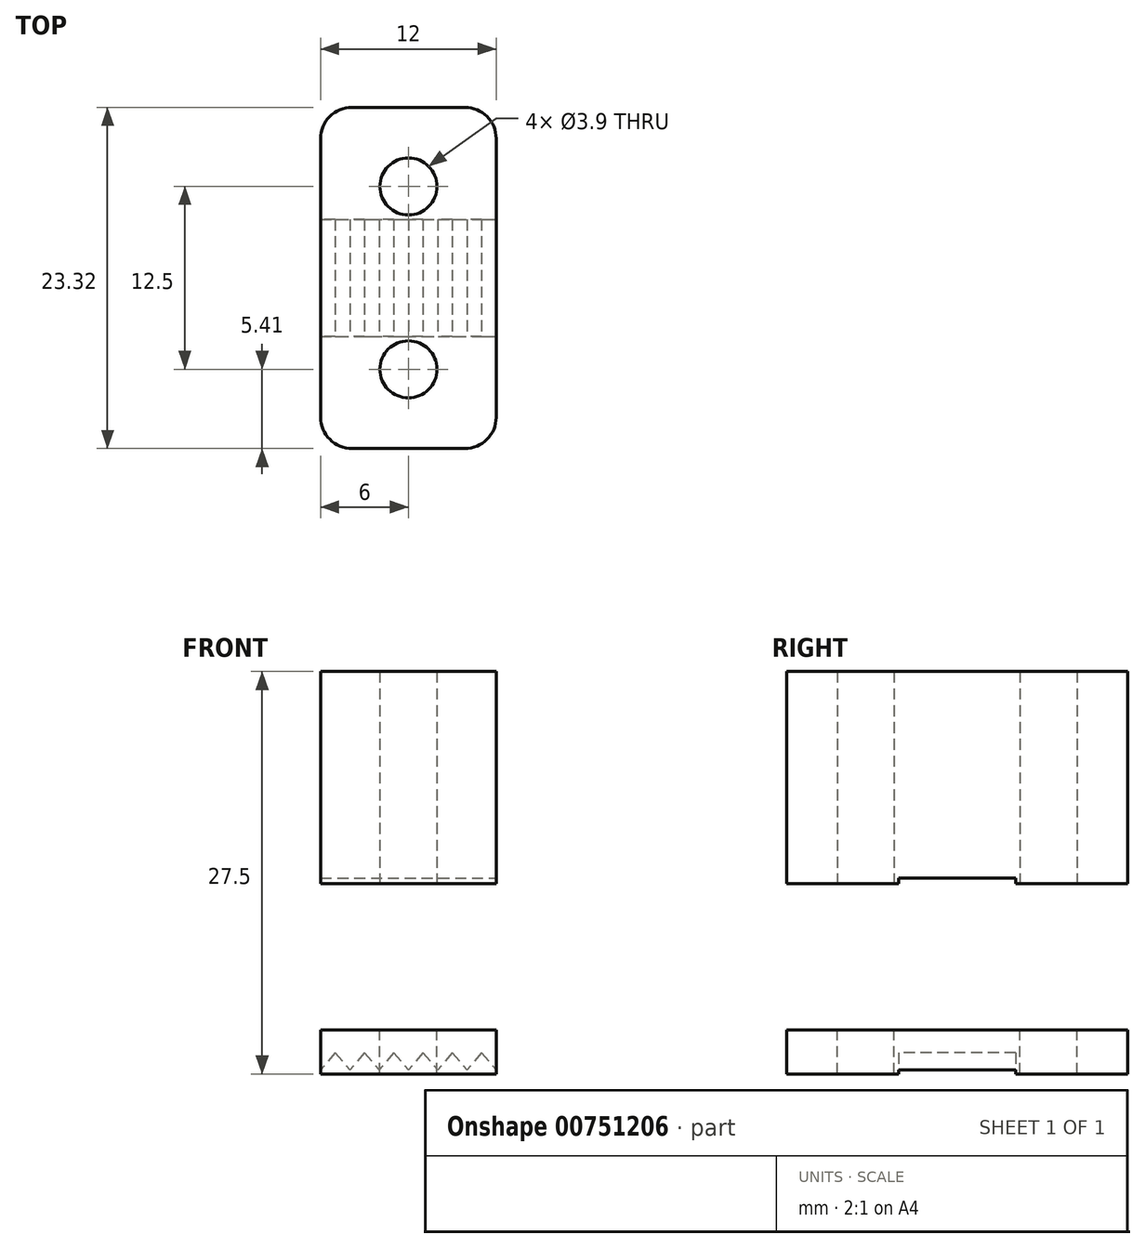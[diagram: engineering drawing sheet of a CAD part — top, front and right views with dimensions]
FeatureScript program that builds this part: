
annotation { "Feature Type Name" : "Feature", "Feature Type Description" : "" }
export const myFeature = defineFeature(function(context is Context, id is Id, definition is map)
    precondition{}
    {
        {
            var Q0;
            Q0=qCreatedBy(makeId("Top.planeOp"),FACE);
            var sketch = newSketch(context, id + "F0", { "sketchPlane" : qUnion([Q0])});
            skCircle(sketch, "E0", {"center": v(0, 6.25) * mm, "radius": 1.95 * mm});
            skLineSegment(sketch, "E1.bottom", {"start": v(-3.85, 11.66) * mm, "end": v(3.85, 11.66) * mm});
            skLineSegment(sketch, "E1.top", {"start": v(-6, 0) * mm, "end": v(6, 0) * mm});
            skLineSegment(sketch, "E1.left", {"start": v(-6, 9.52) * mm, "end": v(-6, 0) * mm});
            skLineSegment(sketch, "E1.right", {"start": v(6, 9.52) * mm, "end": v(6, 0) * mm});
            skPoint(sketch, "E2.visualSharp", {"position": v(-6, 11.66) * mm});
            skArc(sketch, "E2.filletArc", {"start": v(-3.85, 11.66) * mm, "mid": v(-5.37, 11.03) * mm, "end": v(-6, 9.52) * mm});
            skPoint(sketch, "E3.visualSharp", {"position": v(6, 11.66) * mm});
            skArc(sketch, "E3.filletArc", {"start": v(6, 9.52) * mm, "mid": v(5.37, 11.03) * mm, "end": v(3.85, 11.66) * mm});
            skSolve(sketch);
        }
        {
            var Q0;
            Q0=makeQuery(id+"F0.imprint","IMPRINT",FACE,{"disambiguationData":[TD([[makeQuery(id+"F0.imprint","IMPRINT",EDGE,{"derivedFrom":sQuery(id+"F0.wireOp",EDGE,"E0")}),-1.0]])]});
            extrude(context, id + "F1", {"entities" : qUnion([Q0]), "depth" : 6.5 * mm});
        }
        {
            var Q0;
            Q0=makeQuery(id+"F1.opExtrude","SWEPT_BODY",BODY,{"disambiguationData":[OSD([sQuery(id+"F0.wireOp",EDGE,"E0"),sQuery(id+"F0.wireOp",EDGE,"E1.bottom"),sQuery(id+"F0.wireOp",EDGE,"E1.top"),sQuery(id+"F0.wireOp",EDGE,"E1.left"),sQuery(id+"F0.wireOp",EDGE,"E1.right"),sQuery(id+"F0.wireOp",EDGE,"E2.filletArc"),sQuery(id+"F0.wireOp",EDGE,"E3.filletArc")])]});
            var Q1;
            Q1=qCreatedBy(makeId("Front.planeOp"),FACE);
            mirror(context, id + "F2", {"operationType" : NewBodyOperationType.ADD, "entities" : qUnion([Q0]), "mirrorPlane" : qUnion([Q1])});
        }
        {
            var Q0;
            Q0=qCreatedBy(makeId("Top.planeOp"),FACE);
            cPlane(context, id + "F3", {"entities" : qUnion([Q0]), "cplaneType" : CPlaneType.OFFSET, "offset" : 10 * mm, "oppositeDirection" : true, "width" : 150 * mm, "height" : 150 * mm});
        }
        {
            var Q0;
            Q0=qCreatedBy(id+"F3.planeOp",FACE);
            var sketch = newSketch(context, id + "F4", { "sketchPlane" : qUnion([Q0])});
            skCircle(sketch, "E4.0", {"center": v(0, -6.25) * mm, "radius": 1.95 * mm});
            skCircle(sketch, "E5.0", {"center": v(0, 6.25) * mm, "radius": 1.95 * mm});
            skLineSegment(sketch, "E6.0", {"start": v(-6, 9.52) * mm, "end": v(-6, -9.52) * mm});
            skArc(sketch, "E7.0", {"start": v(-3.85, -11.66) * mm, "mid": v(-5.37, -11.03) * mm, "end": v(-6, -9.52) * mm});
            skLineSegment(sketch, "E8.0", {"start": v(-3.85, -11.66) * mm, "end": v(3.85, -11.66) * mm});
            skPoint(sketch, "E9.0", {"position": v(5.37, -11.03) * mm});
            skArc(sketch, "E10.0", {"start": v(6, -9.52) * mm, "mid": v(5.37, -11.03) * mm, "end": v(3.85, -11.66) * mm});
            skLineSegment(sketch, "E11.0", {"start": v(6, 9.52) * mm, "end": v(6, -9.52) * mm});
            skArc(sketch, "E12.0", {"start": v(6, 9.52) * mm, "mid": v(5.37, 11.03) * mm, "end": v(3.85, 11.66) * mm});
            skLineSegment(sketch, "E13.0", {"start": v(-3.85, 11.66) * mm, "end": v(3.85, 11.66) * mm});
            skArc(sketch, "E14.0", {"start": v(-3.85, 11.66) * mm, "mid": v(-5.37, 11.03) * mm, "end": v(-6, 9.52) * mm});
            skSolve(sketch);
        }
        {
            var Q0;
            Q0=makeQuery(id+"F4.imprint","IMPRINT",FACE,{"disambiguationData":[TD([[makeQuery(id+"F4.imprint","IMPRINT",EDGE,{"derivedFrom":sQuery(id+"F4.wireOp",EDGE,"E4.0")}),-1.0]])]});
            extrude(context, id + "F5", {"entities" : qUnion([Q0]), "oppositeDirection" : true, "depth" : 3 * mm});
        }
        {
            var Q0;
            Q0=qCreatedBy(makeId("Front.planeOp"),FACE);
            var sketch = newSketch(context, id + "F6", { "sketchPlane" : qUnion([Q0])});
            skLineSegment(sketch, "E15.0", {"start": v(-6, -13) * mm, "end": v(-6, -12.73) * mm});
            skLineSegment(sketch, "E16.bottom", {"start": v(-6, -13) * mm, "end": v(-4, -13) * mm});
            skLineSegment(sketch, "E16.right", {"start": v(-4, -13) * mm, "end": v(-4, -12.73) * mm});
            skPoint(sketch, "E17", {"position": v(-5, -11.55) * mm});
            skLineSegment(sketch, "E18", {"start": v(-5, -11.55) * mm, "end": v(-4, -12.73) * mm});
            skLineSegment(sketch, "E19", {"start": v(-5, -11.55) * mm, "end": v(-6, -12.73) * mm});
            skPoint(sketch, "E20.orphan", {"position": v(-4, -11.55) * mm});
            skLineSegment(sketch, "E21.trimOffspring", {"start": v(-6, -11.55) * mm, "end": v(-6, -10) * mm});
            skLineSegment(sketch, "E22.1.0.0", {"start": v(-3, -11.55) * mm, "end": v(-2, -12.73) * mm});
            skLineSegment(sketch, "E22.1.0.1", {"start": v(-3, -11.55) * mm, "end": v(-4, -12.73) * mm});
            skLineSegment(sketch, "E22.1.0.3", {"start": v(-4, -13) * mm, "end": v(-2, -13) * mm});
            skLineSegment(sketch, "E22.1.0.4", {"start": v(-2, -13) * mm, "end": v(-2, -12.73) * mm});
            skLineSegment(sketch, "E22.2.0.0", {"start": v(-1, -11.55) * mm, "end": v(0, -12.73) * mm});
            skLineSegment(sketch, "E22.2.0.1", {"start": v(-1, -11.55) * mm, "end": v(-2, -12.73) * mm});
            skLineSegment(sketch, "E22.2.0.2", {"start": v(-2, -13) * mm, "end": v(-2, -12.73) * mm});
            skLineSegment(sketch, "E22.2.0.3", {"start": v(-2, -13) * mm, "end": v(0, -13) * mm});
            skLineSegment(sketch, "E22.2.0.4", {"start": v(0, -13) * mm, "end": v(0, -12.73) * mm});
            skLineSegment(sketch, "E22.3.0.0", {"start": v(1, -11.55) * mm, "end": v(2, -12.73) * mm});
            skLineSegment(sketch, "E22.3.0.1", {"start": v(1, -11.55) * mm, "end": v(0, -12.73) * mm});
            skLineSegment(sketch, "E22.3.0.2", {"start": v(0, -13) * mm, "end": v(0, -12.73) * mm});
            skLineSegment(sketch, "E22.3.0.3", {"start": v(0, -13) * mm, "end": v(2, -13) * mm});
            skLineSegment(sketch, "E22.3.0.4", {"start": v(2, -13) * mm, "end": v(2, -12.73) * mm});
            skLineSegment(sketch, "E22.4.0.0", {"start": v(3, -11.55) * mm, "end": v(4, -12.73) * mm});
            skLineSegment(sketch, "E22.4.0.1", {"start": v(3, -11.55) * mm, "end": v(2, -12.73) * mm});
            skLineSegment(sketch, "E22.4.0.2", {"start": v(2, -13) * mm, "end": v(2, -12.73) * mm});
            skLineSegment(sketch, "E22.4.0.3", {"start": v(2, -13) * mm, "end": v(4, -13) * mm});
            skLineSegment(sketch, "E22.4.0.4", {"start": v(4, -13) * mm, "end": v(4, -12.73) * mm});
            skLineSegment(sketch, "E22.5.0.0", {"start": v(5, -11.55) * mm, "end": v(6, -12.73) * mm});
            skLineSegment(sketch, "E22.5.0.1", {"start": v(5, -11.55) * mm, "end": v(4, -12.73) * mm});
            skLineSegment(sketch, "E22.5.0.2", {"start": v(4, -13) * mm, "end": v(4, -12.73) * mm});
            skLineSegment(sketch, "E22.5.0.3", {"start": v(4, -13) * mm, "end": v(6, -13) * mm});
            skLineSegment(sketch, "E22.5.0.4", {"start": v(6, -13) * mm, "end": v(6, -12.73) * mm});
            skLineSegment(sketch, "E22.direction1", {"start": v(-4, -12.73) * mm, "end": v(-2, -12.73) * mm, "construction": true});
            skSolve(sketch);
        }
        {
            var Q0;
            Q0=qSketchRegion(id+"F6",true);
            extrude(context, id + "F7", {"entities" : qUnion([Q0]), "operationType" : NewBodyOperationType.REMOVE, "oppositeDirection" : true, "depth" : 4 * mm, "hasSecondDirection" : true, "secondDirectionOppositeDirection" : false, "secondDirectionDepth" : 4 * mm});
        }
        {
            var Q0;
            Q0=qCreatedBy(makeId("Top.planeOp"),FACE);
            var sketch = newSketch(context, id + "F8", { "sketchPlane" : qUnion([Q0])});
            skLineSegment(sketch, "E23.0", {"start": v(-6, 9.52) * mm, "end": v(-6, -9.52) * mm});
            skLineSegment(sketch, "E24.0", {"start": v(6, 9.52) * mm, "end": v(6, -9.52) * mm});
            skLineSegment(sketch, "E25.bottom", {"start": v(-6, 4) * mm, "end": v(6, 4) * mm});
            skLineSegment(sketch, "E25.top", {"start": v(-6, 0) * mm, "end": v(6, 0) * mm});
            skLineSegment(sketch, "E25.left", {"start": v(-6, 4) * mm, "end": v(-6, 0) * mm});
            skLineSegment(sketch, "E25.right", {"start": v(6, 4) * mm, "end": v(6, 0) * mm});
            skLineSegment(sketch, "E26.MirrorCS", {"start": v(-6, -4) * mm, "end": v(6, -4) * mm});
            skSolve(sketch);
        }
        {
            var Q0;
            Q0=makeQuery(id+"F8.imprint","IMPRINT",FACE,{"disambiguationData":[TD([[makeQuery(id+"F8.imprint","IMPRINT",EDGE,{"derivedFrom":sQuery(id+"F8.wireOp",EDGE,"E25.bottom")}),-1.0]])]});
            var Q1;
            {var subQ0=sQuery(id+"F8.wireOp",EDGE,"E25.top");Q1=makeQuery(id+"F8.imprint","IMPRINT",FACE,{"disambiguationData":[TD([[makeQuery(id+"F8.imprint","IMPRINT",EDGE,{"derivedFrom":subQ0}),-1.0]])]});}
            extrude(context, id + "F9", {"entities" : qUnion([Q0, Q1]), "operationType" : NewBodyOperationType.REMOVE, "depth" : 0.4 * mm});
        }
        {
            var Q0;
            {var subQ0=makeQuery(id+"F1.opExtrude","CAP_FACE",FACE,{"disambiguationData":[OSD([sQuery(id+"F0.wireOp",EDGE,"E0"),sQuery(id+"F0.wireOp",EDGE,"E1.bottom"),sQuery(id+"F0.wireOp",EDGE,"E1.top"),sQuery(id+"F0.wireOp",EDGE,"E1.left"),sQuery(id+"F0.wireOp",EDGE,"E1.right"),sQuery(id+"F0.wireOp",EDGE,"E2.filletArc"),sQuery(id+"F0.wireOp",EDGE,"E3.filletArc")])],"isStart":false});Q0=makeQuery(id+"F2.boolean.opBoolean","MERGE",FACE,{"derivedFrom":[subQ0,makeQuery(id+"F2.opPattern","COPY",FACE,{"derivedFrom":subQ0,"instanceName":"1"})]});}
            extrude(context, id + "F10", {"entities" : qUnion([Q0]), "operationType" : NewBodyOperationType.ADD, "depth" : 8 * mm, "offsetDistance" : 25 * mm});
        }
    });
